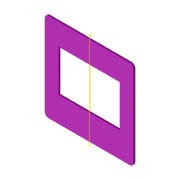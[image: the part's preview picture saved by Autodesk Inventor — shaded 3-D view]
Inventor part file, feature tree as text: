
AUTODESK INVENTOR PART (.ipt)
format: ipt  version: 2022 (Build 260153000, 153)  size: 97,792 bytes
history: native  units: mm
features: extrude x1, plane x1, sketch x1
ambient origin geometry x8: Origin, YZ Plane, XZ Plane, XY Plane, X Axis, Y Axis, Z Axis, Center Point
bodies: Volumenkörper1 (feature_tree)
feature tree (3):
  extrude  "Extrusion1"  Depth=51.0mm
  plane  "Arbeitsebene1"
  sketch  "Skizze1"  dims[d0=51.0mm d1=51.0mm d2=35.0mm d3=24.0mm d4=12.5mm d5=2.0mm d6=1.0mm d7=0.0mm]
